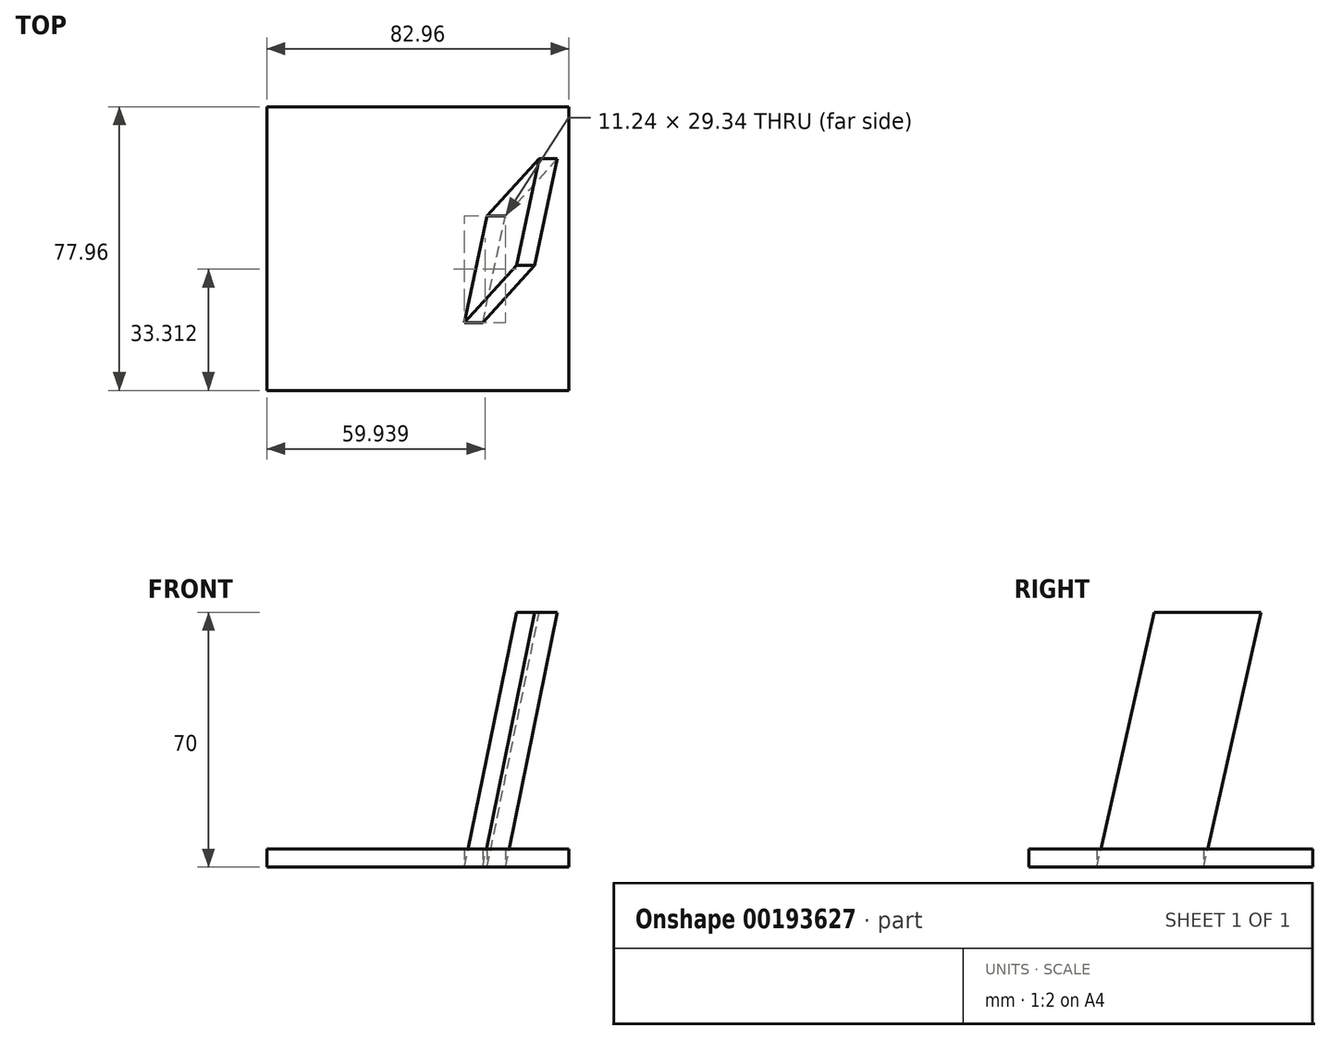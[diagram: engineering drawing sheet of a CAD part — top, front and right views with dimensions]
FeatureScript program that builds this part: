
annotation { "Feature Type Name" : "Feature", "Feature Type Description" : "" }
export const myFeature = defineFeature(function(context is Context, id is Id, definition is map)
    precondition{}
    {
        {
            var Q0;
            Q0=qCreatedBy(makeId("Top.planeOp"),FACE);
            var sketch = newSketch(context, id + "F0", { "sketchPlane" : qUnion([Q0])});
            skLineSegment(sketch, "E0.bottom", {"start": v(41.48, -38.98) * mm, "end": v(-41.48, -38.98) * mm});
            skLineSegment(sketch, "E0.top", {"start": v(41.48, 38.98) * mm, "end": v(-41.48, 38.98) * mm});
            skLineSegment(sketch, "E0.left", {"start": v(41.48, -38.98) * mm, "end": v(41.48, 38.98) * mm});
            skLineSegment(sketch, "E0.right", {"start": v(-41.48, -38.98) * mm, "end": v(-41.48, 38.98) * mm});
            skPoint(sketch, "E0.middle", {"position": v(0, 0) * mm});
            skLineSegment(sketch, "E1", {"start": v(12.84, -20.34) * mm, "end": v(17.84, -20.34) * mm});
            skLineSegment(sketch, "E2", {"start": v(17.84, -20.34) * mm, "end": v(24.08, 9) * mm});
            skLineSegment(sketch, "E3", {"start": v(24.08, 9) * mm, "end": v(19.08, 9) * mm});
            skLineSegment(sketch, "E4", {"start": v(19.08, 9) * mm, "end": v(12.84, -20.34) * mm});
            skSolve(sketch);
        }
        {
            var Q0;
            Q0=makeQuery(id+"F0.imprint","IMPRINT",FACE,{"disambiguationData":[TD([[makeQuery(id+"F0.imprint","IMPRINT",EDGE,{"derivedFrom":sQuery(id+"F0.wireOp",EDGE,"E0.bottom")}),-1.0]])]});
            cPlane(context, id + "F1", {"entities" : qUnion([Q0]), "cplaneType" : CPlaneType.OFFSET, "offset" : 70 * mm, "width" : 150 * mm, "height" : 150 * mm});
        }
        {
            var Q0;
            Q0=qCreatedBy(id+"F1.planeOp",FACE);
            var sketch = newSketch(context, id + "F2", { "sketchPlane" : qUnion([Q0])});
            skLineSegment(sketch, "E5.0", {"start": v(33.38, 24.7) * mm, "end": v(27.14, -4.64) * mm});
            skLineSegment(sketch, "E5.1", {"start": v(38.38, 24.7) * mm, "end": v(33.38, 24.7) * mm});
            skLineSegment(sketch, "E5.2", {"start": v(32.14, -4.64) * mm, "end": v(38.38, 24.7) * mm});
            skLineSegment(sketch, "E5.3", {"start": v(27.14, -4.64) * mm, "end": v(32.14, -4.64) * mm});
            skSolve(sketch);
        }
        {
            var Q0;
            Q0=makeQuery(id+"F0.imprint","IMPRINT",FACE,{"disambiguationData":[TD([[makeQuery(id+"F0.imprint","IMPRINT",EDGE,{"derivedFrom":sQuery(id+"F0.wireOp",EDGE,"E1")}),1.0]])]});
            var Q1;
            Q1=makeQuery(id+"F2.imprint","IMPRINT",FACE,{"disambiguationData":[TD([[makeQuery(id+"F2.imprint","IMPRINT",EDGE,{"derivedFrom":sQuery(id+"F2.wireOp",EDGE,"E5.0")}),1.0]])]});
            loft(context, id + "F3", {"sheetProfilesArray" : [{ "sheetProfileEntities" : qUnion([Q0]) }, { "sheetProfileEntities" : qUnion([Q1]) }]});
        }
        {
            var Q0;
            Q0=makeQuery(id+"F0.imprint","IMPRINT",FACE,{"disambiguationData":[TD([[makeQuery(id+"F0.imprint","IMPRINT",EDGE,{"derivedFrom":sQuery(id+"F0.wireOp",EDGE,"E0.bottom")}),-1.0]])]});
            extrude(context, id + "F4", {"entities" : qUnion([Q0]), "depth" : 5 * mm});
        }
        {
            var Q0;
            Q0=makeQuery(id+"F3.opLoft","CAP_FACE",FACE,{"disambiguationData":[OSD([makeQuery(id+"F2.imprint","IMPRINT",FACE,{"disambiguationData":[TD([[makeQuery(id+"F2.imprint","IMPRINT",EDGE,{"derivedFrom":sQuery(id+"F2.wireOp",EDGE,"E5.0")}),1.0]])]})])],"isStart":true});
            var sketch = newSketch(context, id + "F5", { "sketchPlane" : qUnion([Q0])});
            skLineSegment(sketch, "E6", {"start": v(30.26, 10.03) * mm, "end": v(35.26, 10.03) * mm, "construction": true});
            skSolve(sketch);
        }
    });
